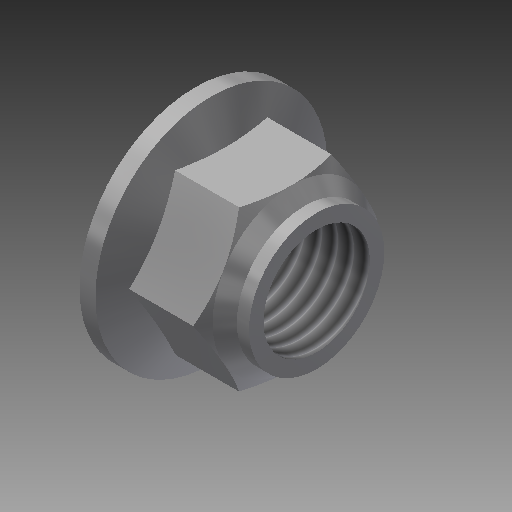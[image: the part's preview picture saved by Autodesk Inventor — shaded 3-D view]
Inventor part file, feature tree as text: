
AUTODESK INVENTOR PART (.ipt)
format: ipt  version: 2019 (Build 230136000, 136)  size: 177,664 bytes
history: native  units: mm
features: sketch x3, revolve x2, extrude x1, thread x1, reference x1
ambient origin geometry x8: Origin, YZ Plane, XZ Plane, XY Plane, X Axis, Y Axis, Z Axis, Center Point
bodies: Solid1 (feature_tree)
feature tree (8):
  extrude  "Extrusion1"  Depth=10.0mm TaperAngle=0.0deg
  revolve  "Revolution1"  Angle=22.5deg
  revolve  "Revolution2"  Angle=90.0deg
  thread  "Thread1"  [1 undecoded]
  sketch  "Sketch2"  dims[d1=10.0mm d2=11.4mm d3=0.0mm]
  sketch  "Sketch3"  dims[d4=1.5mm d5=22.5deg]
  reference  "Reference6"
  sketch  "Sketch4"  dims[d6=5.0mm d7=90.0deg d8=135.0deg d9=1.14mm d10=6.36mm d11=120.0deg d12=2.28mm d13=3.0mm d14=90.0deg d15=10.0mm d16=0.0mm]
note: 1 required parameter value undecoded (feature->parameter linkage not recoverable at this tier; creation-order binding heuristic only, values carry confidence <= 0.55)
